# Revit family: IS_Idealrain_BC807_BIM_NL
name_source: partatom
category: Plumbing Fixtures
units: mm (PartAtom-declared; Revit-internal decimal feet)

## family parameters
Always vertical = No
Cut with Voids When Loaded = No
OmniClass Number = 23.45.55.00
OmniClass Title = Sanitary Faucets, Wastes
Part Type = Normal
Room Calculation Point = No
Round Connector Dimension = Use Diameter
Shared = No
Work Plane-Based = No

## types (5) — shared parameters
Accesoires = https://www.idealstandard.nl
Accessories = https://www.idealstandard.nl
Afmetingen = 60 x 58 x 63 mm
AfstandsEenheid = Millimeter
AreaUnits = Millimetres
Artikelomschrijving = IDEALRAIN WANDHALTERUNG ZYLINDRISCH 1/2''ANSCHLUSS
Artikelreferentie = IDEALRAIN WALL BRACKETCYLINDRICAL 1/2''CONN
Auteur = Ideal Standard
BIMObjectName = IS_IdealStandard_Showermixers_Idealrain_BC807
BIMobject category = Sanitary
BIMobject category code = Taps & Mixers
BIMobject main category = Sanitary
Beschrijvinggarantie = Herstellergarantie
BimObjectNaam = IS_IdealStandard_Showermixers_Idealrain_BC807
Brand = Ideal Standard
Brand url = http://www.idealstandard.nl
Breedte = 60
ConnectionType = Installation
CurrencyUnit = €
CurrentRevision = 1
Date of publishing = 24/07/2021
Diepte = 58 mm  [stored 0.190289 ft]
Douchebak = No
DurationUnit = Years
Edition number = 1
Garantieonderdelen = 5
Garantieunits = Jaren
GemaaktOp = 27/07/2021
HasIntegralShutOffDevice = No
Help = https://www.idealstandard.nl
Hoogte = 63.022133
Hulp = https://www.idealstandard.nl
IFC Classification = Sanitary Terminal
IfcExportAs = IfcValveType
IfcExportType = MIXING
Installatieinstructies = https://www.idealstandard.nl
Installation instructions = https://www.idealstandard.nl
InstallationInstructions = https://www.idealstandard.nl
IsBuiltIn = No
IsHighPressure = No
LinearUnits = Millimetres
MaintenanceInformation = https://www.idealstandard.nl
Manufacturer = Ideal Standard
Manufacturer name = Ideal Standard
ManufacturerURL = https://www.idealstandard.nl
Materiaal = Messing
Material = Brass
Material main = Brass
Merk = Ideal Standard
ModelReference = IDEALRAIN WALL BRACKETCYLINDRICAL 1/2''CONN
Montageinstuctie = https://www.idealstandard.nl
NBS Reference Code = 45-35-70/335
NBS Reference Description = Shower mixers
Name = Showermixers_Idealrain_BC807_IdealStandard
NettWeight = 0.19
Nettogewicht = 0.19
NominalDepth = 58 mm  [stored 0.190289 ft]
NominalHeight = 63 mm
NominalLength = 58 mm  [stored 0.190289 ft]
NominalWidth = 60 mm  [stored 0.19685 ft]
Normen = Showermixers_Idealrain_BC807_IdealStandard
OppervlakteEenheid = Millimeter
Product Guid = bee6da3b-7bcf-4e8b-b05f-1c6dd15d2ed4
Product SKU = BC807
Product certification = https://www.idealstandard.nl
Product data url = https://bimobject.com
Product family = Sanitary
Product group = Showers
Product name = IDEALRAIN WALL BRACKET CYLINDRICAL
Product url = https://www.idealstandard.nl
ProductInformation = https://www.idealstandard.nl
ProductSoort = Sanitary
Productinformatie = https://www.idealstandard.nl
QR code = http://bimobject.com
Referentie = IDEALRAIN WALL BRACKETCYLINDRICAL 1/2''CONN
Revisie = 1
Shape = Cylindrical
Size = 60 x 58 x 63 mm
Space = Internal
SpareParts = https://www.idealstandard.nl
Technical description = https://www.idealstandard.nl
Telefoonnummer = 077 355 08 08
TestPressure = 10 Bar
Testdruk = 10 Bar
Typeconnectie = Installation
URL = https://www.idealstandard.nl
Uniclass 2015 Code = Pr_40_20_87_80
Uniclass 2015 Name = Shower thermostatic valves
Uniclass2015Beschrijving = Shower thermostatic valves
Uniclass2015Code = Pr_40_20_87_80
Uniclass2015Referentie = Pr_40_20_87_80
Uniclass2015Title = Shower thermostatic valves
Uniclass2015Version = v1.22
Urlproducent = https://www.idealstandard.nl
ValutaEenheid = Euro
Versie = 1
Version = 1
VolumeUnits = Litres
Volumeunits = Liters
Vorm = zylindrisch
WRASURL = https://www.wrasapprovals.co.uk
WarrantyDescription = Manufacturer warranty
WarrantyDurationUnit = Years
Wisselstukken = https://www.idealstandard.nl
Youtube clip = https://www.youtube.com
zero-valued in all types: BrutoGewicht, Cost, Lengte, Vervangingskosten

## per-type parameters (varying)
| type | Afwerking | Artikelnummer | BarCode | Barcode | Color | Description | Eigenschappen | Features | Finish | GTIN code | Kleur | MainColor | Model | ModelNumber |
| BC807AA - IDEALRAIN WALL BRACKETCYLINDRICAL 1/2''CONN - CHROME | Chrom | BC807AA | 3800861086338 | 3800861086338 | Chrom | IDEALRAIN WANDHALTERUNG ZYLINDRISCH 1/2''ANSCHLUSS - CHROM | WANDHALTERUNG ZYLINDRISCH 1/2''ANSCHLUSS - CHROM | WANDHALTERUNG ZYLINDRISCH 1/2''ANSCHLUSS - CHROM | Chrom | https://3800861086338 | Chrom | Chrom | BC807AA | BC807AA |
| BC807A5 - IDEALRAIN WALL BRACKETCYLINDRICAL 1/2''CONN - MAGNETIC GREY | magnetisch grau | BC807A5 | 3800861087533 | 3800861087533 | magnetisch grau | IDEALRAIN WANDHALTERUNG ZYLINDRISCH 1/2''ANSCHLUSS - MAGNETISCHES GRAU | WANDHALTERUNG ZYLINDRISCH 1/2''ANSCHLUSS - MAGNETISCHES GRAU | WANDHALTERUNG ZYLINDRISCH 1/2''ANSCHLUSS - MAGNETISCHES GRAU | magnetisch grau | https://3800861087533 | magnetisch grau | magnetisch grau | BC807A5 | BC807A5 |
| BC807XG - IDEALRAIN WALL BRACKETCYLINDRICAL 1/2''CONN - SILK BLACK | Seide schwarz | BC807XG | 3800861101185 | 3800861101185 | Seide schwarz | IDEALRAIN WANDHALTERUNG ZYLINDRISCH 1/2''ANSCHLUSS - SEIDE SCHWARZ | WANDHALTERUNG ZYLINDRISCH 1/2''ANSCHLUSS - SEIDE SCHWARZ | WANDHALTERUNG ZYLINDRISCH 1/2''ANSCHLUSS - SEIDE SCHWARZ | Seide schwarz | https://3800861101185 | Seide schwarz | Seide schwarz | BC807XG | BC807XG |
| BC807GN - IDEALRAIN WALL BRACKETCYLINDRICAL 1/2''CONN - SILVER STORM | silberner Sturm | BC807GN | 3800861086734 | 3800861086734 | silberner Sturm | IDEALRAIN WANDHALTERUNG ZYLINDRISCH 1/2''ANSCHLUSS - SILBER STURM | WANDHALTERUNG ZYLINDRISCH 1/2''ANSCHLUSS - SILBER STURM | WANDHALTERUNG ZYLINDRISCH 1/2''ANSCHLUSS - SILBER STURM | silberner Sturm | https://3800861086734 | silberner Sturm | silberner Sturm | BC807GN | BC807GN |
| BC807A2 - IDEALRAIN WALL BRACKETCYLINDRICAL 1/2''CONN - BRUSH GOLD | Pinsel gold | BC807A2 | 3800861087137 | 3800861087137 | Pinsel gold | IDEALRAIN WANDHALTERUNG ZYLINDRISCH 1/2''ANSCHLUSS - PINSEL GOLD | WANDHALTERUNG ZYLINDRISCH 1/2''ANSCHLUSS - PINSEL GOLD | WANDHALTERUNG ZYLINDRISCH 1/2''ANSCHLUSS - PINSEL GOLD | Pinsel gold | https://3800861087137 | Pinsel gold | Pinsel gold | BC807A2 | BC807A2 |

note: [stored X ft] marks values corroborated as IEEE doubles in the binary element streams (Revit-internal decimal feet)

## geometry (parser evidence)
native form markers: Sweep x4
no freeform markers — native parametric forms only
